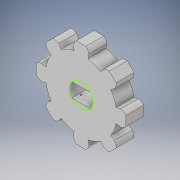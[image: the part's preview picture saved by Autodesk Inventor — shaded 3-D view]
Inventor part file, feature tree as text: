
AUTODESK INVENTOR PART (.ipt)
format: ipt  version: 2017 (Build 210142000, 142)  size: 174,080 bytes
history: native  units: in
note: dims shown in document units (in); Inventor stores cm internally (conversion verified against a paired STEP export)
features: sketch x3, extrude x2, pattern_circular x1
ambient origin geometry x8: Origin, YZ Plane, XZ Plane, XY Plane, X Axis, Y Axis, Z Axis, Center Point
bodies: Solid1 (feature_tree)
feature tree (6):
  extrude  "Extrusion1"  Depth=0.15in TaperAngle=360.0deg
  pattern_circular  "Circular Pattern1"  [2 undecoded]
  extrude  "Extrusion3"  [1 undecoded]
  sketch  "Sketch4"  dims[d14=0.0591in d15=1.0in d16=0.0in]
  sketch  "Sketch1"  dims[d0=0.6in d1=360.0deg d2=0.04in d3=0.04in d4=0.075in d5=0.15in d6=0.0in d7=3.1496in d8=360.0deg]
  sketch  "Sketch3"  dims[d13=0.1969in]
note: 3 required parameter values undecoded (feature->parameter linkage not recoverable at this tier; creation-order binding heuristic only, values carry confidence <= 0.55)
